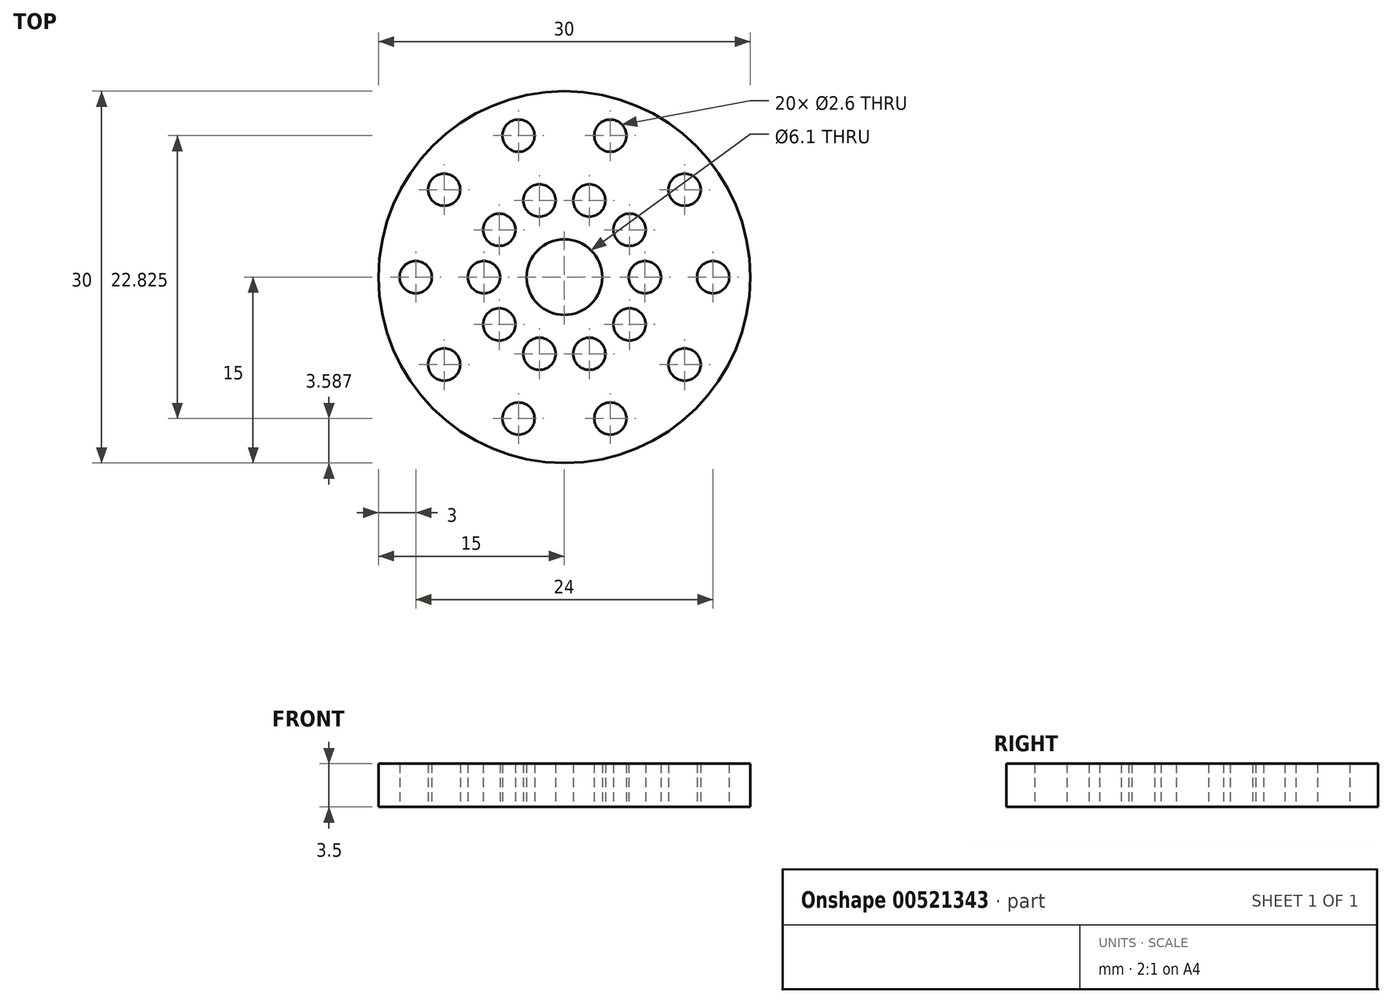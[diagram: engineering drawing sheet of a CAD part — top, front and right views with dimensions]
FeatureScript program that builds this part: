
annotation { "Feature Type Name" : "Feature", "Feature Type Description" : "" }
export const myFeature = defineFeature(function(context is Context, id is Id, definition is map)
    precondition{}
    {
        {
            var Q0;
            Q0=qCreatedBy(makeId("Top.planeOp"),FACE);
            var sketch = newSketch(context, id + "F0", { "sketchPlane" : qUnion([Q0])});
            skCircle(sketch, "E0", {"center": v(0, 0) * mm, "radius": 3.05 * mm});
            skCircle(sketch, "E1.0", {"center": v(0, 0) * mm, "radius": 15 * mm});
            skCircle(sketch, "E2", {"center": v(-12, 0) * mm, "radius": 1.3 * mm});
            skCircle(sketch, "E3", {"center": v(-6.5, 0) * mm, "radius": 1.3 * mm});
            skLineSegment(sketch, "E4.anchor1", {"start": v(0, 0) * mm, "end": v(-6.5, 0) * mm, "construction": true});
            skLineSegment(sketch, "E4.anchor2", {"start": v(0, 0) * mm, "end": v(-6.5, 0) * mm, "construction": true});
            skCircle(sketch, "E5.0.1.0", {"center": v(-5.26, -3.82) * mm, "radius": 1.3 * mm});
            skCircle(sketch, "E5.1.1.0", {"center": v(-9.7, -7.05) * mm, "radius": 1.3 * mm});
            skCircle(sketch, "E5.0.2.0", {"center": v(-2, -6.18) * mm, "radius": 1.3 * mm});
            skCircle(sketch, "E5.1.2.0", {"center": v(-3.7, -11.41) * mm, "radius": 1.3 * mm});
            skCircle(sketch, "E5.0.3.0", {"center": v(2, -6.18) * mm, "radius": 1.3 * mm});
            skCircle(sketch, "E5.1.3.0", {"center": v(3.7, -11.41) * mm, "radius": 1.3 * mm});
            skCircle(sketch, "E5.0.4.0", {"center": v(5.26, -3.82) * mm, "radius": 1.3 * mm});
            skCircle(sketch, "E5.1.4.0", {"center": v(9.7, -7.05) * mm, "radius": 1.3 * mm});
            skCircle(sketch, "E5.0.5.0", {"center": v(6.5, 0) * mm, "radius": 1.3 * mm});
            skCircle(sketch, "E5.1.5.0", {"center": v(12, 0) * mm, "radius": 1.3 * mm});
            skCircle(sketch, "E5.0.6.0", {"center": v(5.26, 3.82) * mm, "radius": 1.3 * mm});
            skCircle(sketch, "E5.1.6.0", {"center": v(9.7, 7.05) * mm, "radius": 1.3 * mm});
            skCircle(sketch, "E5.0.7.0", {"center": v(2, 6.18) * mm, "radius": 1.3 * mm});
            skCircle(sketch, "E5.1.7.0", {"center": v(3.7, 11.41) * mm, "radius": 1.3 * mm});
            skCircle(sketch, "E5.0.8.0", {"center": v(-2, 6.18) * mm, "radius": 1.3 * mm});
            skCircle(sketch, "E5.1.8.0", {"center": v(-3.7, 11.41) * mm, "radius": 1.3 * mm});
            skCircle(sketch, "E5.0.9.0", {"center": v(-5.26, 3.82) * mm, "radius": 1.3 * mm});
            skCircle(sketch, "E5.1.9.0", {"center": v(-9.7, 7.05) * mm, "radius": 1.3 * mm});
            skSolve(sketch);
        }
        {
            var Q0;
            Q0 = qSketchRegion(id + "F0", true);
            extrude(context, id + "F1", {"entities" : qUnion([Q0]), "depth" : 3.5 * mm, "offsetDistance" : 25 * mm});
        }
    });
